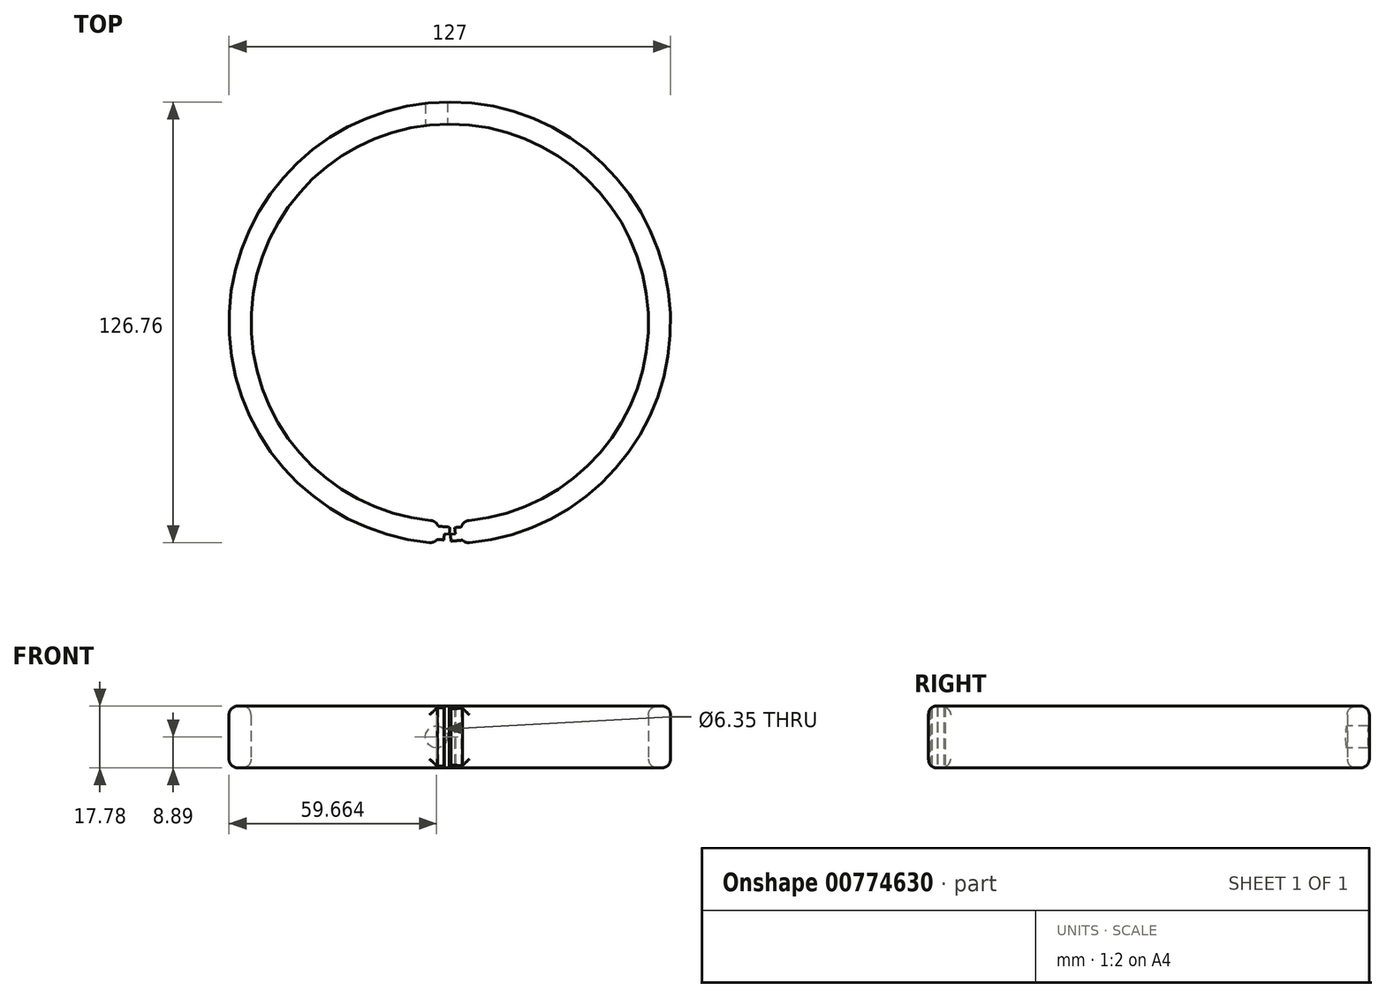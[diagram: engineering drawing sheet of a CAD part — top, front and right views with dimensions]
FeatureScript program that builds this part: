
annotation { "Feature Type Name" : "Feature", "Feature Type Description" : "" }
export const myFeature = defineFeature(function(context is Context, id is Id, definition is map)
    precondition{}
    {
        {
            var Q0;
            Q0=qCreatedBy(makeId("Top.planeOp"),FACE);
            var sketch = newSketch(context, id + "F0", { "sketchPlane" : qUnion([Q0])});
            skArc(sketch, "E0", {"start": v(3.7, -63.4) * mm, "mid": v(0, 63.5) * mm, "end": v(-3.7, -63.4) * mm});
            skArc(sketch, "E1", {"start": v(3.2, -57.06) * mm, "mid": v(0, 57.15) * mm, "end": v(-3.2, -57.06) * mm});
            skLineSegment(sketch, "E2", {"start": v(3.2, -57.06) * mm, "end": v(3.7, -63.4) * mm});
            skLineSegment(sketch, "E3.MirrorCS", {"start": v(-3.2, -57.06) * mm, "end": v(-3.7, -63.4) * mm});
            skPoint(sketch, "E4.start.orphan", {"position": v(0, -57.15) * mm});
            skLineSegment(sketch, "E5", {"start": v(-3.31, -58.53) * mm, "end": v(0, -58.8) * mm});
            skLineSegment(sketch, "E6", {"start": v(0, -58.8) * mm, "end": v(-0.16, -60.83) * mm});
            skLineSegment(sketch, "E7", {"start": v(-0.16, -60.83) * mm, "end": v(-1.56, -60.72) * mm});
            skLineSegment(sketch, "E8", {"start": v(-1.56, -60.72) * mm, "end": v(-1.7, -62.48) * mm});
            skLineSegment(sketch, "E9", {"start": v(-1.7, -62.48) * mm, "end": v(-3.62, -62.32) * mm});
            skPoint(sketch, "E10.start.orphan", {"position": v(0.65, -64.47) * mm});
            skLineSegment(sketch, "E11", {"start": v(3.68, -62.54) * mm, "end": v(0.37, -62.84) * mm});
            skLineSegment(sketch, "E12", {"start": v(0.37, -62.84) * mm, "end": v(0.18, -60.81) * mm});
            skLineSegment(sketch, "E13", {"start": v(0.18, -60.81) * mm, "end": v(1.57, -60.69) * mm});
            skLineSegment(sketch, "E14", {"start": v(1.57, -60.69) * mm, "end": v(1.41, -58.93) * mm});
            skLineSegment(sketch, "E15", {"start": v(1.41, -58.93) * mm, "end": v(3.33, -58.75) * mm});
            skPoint(sketch, "E16", {"position": v(-3.8, 63.39) * mm});
            skPoint(sketch, "E17", {"position": v(8.16, 62.97) * mm});
            skPoint(sketch, "E18", {"position": v(2.86, 63.44) * mm});
            skSolve(sketch);
        }
        {
            var Q0;
            Q0=qCreatedBy(makeId("Front.planeOp"),FACE);
            var sketch = newSketch(context, id + "F1", { "sketchPlane" : qUnion([Q0])});
            skCircle(sketch, "E19", {"center": v(-3.84, 0) * mm, "radius": 3.18 * mm});
            skLineSegment(sketch, "E20", {"start": v(8.16, 1.7) * mm, "end": v(8.16, -2.06) * mm});
            skLineSegment(sketch, "E21", {"start": v(8.16, -2.06) * mm, "end": v(2.86, -2.06) * mm});
            skLineSegment(sketch, "E22", {"start": v(2.86, -2.06) * mm, "end": v(2.86, 1.7) * mm});
            skLineSegment(sketch, "E23", {"start": v(2.86, 1.7) * mm, "end": v(8.16, 1.7) * mm});
            skSolve(sketch);
        }
        {
            var Q0;
            Q0 = qSketchRegion(id + "F0", true);
            extrude(context, id + "F2", {"entities" : qUnion([Q0]), "endBound" : BoundingType.SYMMETRIC, "depth" : 17.78 * mm, "offsetDistance" : 25.4 * mm});
        }
        {
            var Q0;
            Q0=makeQuery(id+"F2.opExtrude","SWEPT_FACE",FACE,{"disambiguationData":[OSD([sQuery(id+"F0.wireOp",EDGE,"E0")])]});
            fillet(context, id + "F3", {"entities" : qUnion([Q0]), "radius" : 2.54 * mm, "tangentPropagation" : true, "allowEdgeOverflow" : false});
        }
        {
            var Q0;
            Q0=makeQuery(id+"F2.opExtrude","SWEPT_FACE",FACE,{"disambiguationData":[OSD([sQuery(id+"F0.wireOp",EDGE,"E1")])]});
            fillet(context, id + "F4", {"entities" : qUnion([Q0]), "radius" : 2.54 * mm, "tangentPropagation" : true, "allowEdgeOverflow" : false});
        }
        {
            var Q0;
            Q0=sQuery(id+"F1.wireOp",VERTEX,"E19.center");
            var Q1;
            Q1=makeQuery(id+"F2.opExtrude","SWEPT_BODY",BODY,{"disambiguationData":[OSD([sQuery(id+"F0.wireOp",EDGE,"E0"),sQuery(id+"F0.wireOp",EDGE,"E1"),sQuery(id+"F0.wireOp",EDGE,"E2"),sQuery(id+"F0.wireOp",EDGE,"E3.MirrorCS"),sQuery(id+"F0.wireOp",EDGE,"E5"),sQuery(id+"F0.wireOp",EDGE,"E6"),sQuery(id+"F0.wireOp",EDGE,"E7"),sQuery(id+"F0.wireOp",EDGE,"E8"),sQuery(id+"F0.wireOp",EDGE,"E9"),sQuery(id+"F0.wireOp",EDGE,"E11"),sQuery(id+"F0.wireOp",EDGE,"E12"),sQuery(id+"F0.wireOp",EDGE,"E13"),sQuery(id+"F0.wireOp",EDGE,"E14"),sQuery(id+"F0.wireOp",EDGE,"E15")])]});
            hole(context, id + "F5", {"style" : HoleStyle.SIMPLE, "endStyle" : HoleEndStyle.THROUGH, "holeDiameter" : 6.35 * mm, "majorDiameter" : 6.35 * mm, "isTappedThrough" : true, "tappedDepth" : 12.7 * mm, "tapClearance" : 3, "locations" : qUnion([Q0]), "scope" : qUnion([Q1])});
        }
    });
